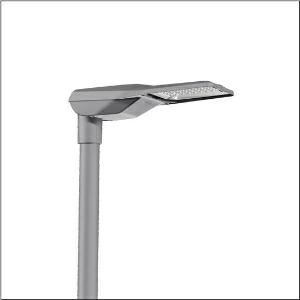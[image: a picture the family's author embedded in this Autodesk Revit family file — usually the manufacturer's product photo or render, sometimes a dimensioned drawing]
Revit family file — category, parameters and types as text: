
# Revit family: streetlight_sl_21_iq_mini___st0_8a_5xe2c41g08jb_e7d2
name_source: partatom
category: Lighting Fixtures
units: mm (PartAtom-declared; Revit-internal decimal feet)

## family parameters
Cut with Voids When Loaded = No
Host = Face
Light Source = No
Part Type = Normal
Room Calculation Point = No
Round Connector Dimension = Use Diameter
Shared = No

## types (1)
- --- (1 x LED, 11290 lm, 71.6 W, 4000K)
    Apparent Load = 72 VA
    CIE Flux Codes = 41 75 97 100 100
    Color Rendering = 70
    Color Temperature = 4000K
    Default Elevation = 1800 mm
    Description = Streetlight SL 21 iQ mini, mast luminaire, primary light control with lens, of PMMA, primary optical cover: cover, of toughened safety glass, transparent, light distribution: ST0.8a, light emission: direct distribution, primary light characteristic: asymmetric, installation type: post-top, side-entry, LED, High Power LED, rated luminous flux: 11.290lm, luminous efficacy: 158lm/W, light colour: 740, colour temperature: 4000K, control: Street-Remote, Auto-Match, Temp-Guard, Lumen-Switch, Night-Set, Smart-Wire, Light-Fading, Desk-Remote (wireless, voltage-free reading and setting of iQ features in the workshop via application-optimized NFC function/RFID function), optimised constant luminous flux control (CLO 2.0), presetting dimming linear, mains connection: 220..240V, AC, 50/60Hz, start of lifetime: 72W, end of service life: 75W, reduction: 33W, luminaire housing, of diecast aluminium, powder-coated, Siteco® metallic grey (DB 702S), corrosivity category C5 mid according to DIN EN ISO 12944, please order mast flange separately, inclination adjustable: 0°, 5°, 10°, 15°, sealing non-destructively replaceable, multi-level sealing system, length: 628mm, width: 235mm, height: 110mm, mast flange for spigot size: 42mm (side-entry): 5XC10008XM4, 60/48mm (side-entry/post-top): 5XC10108XM2, 76/60mm (side-entry/post-top): 5XC10108XM1, protection rating (complete): IP66, insulation class (complete): insulation class II (safety insulation), certification: CE, ENEC, ENEC+, VDE, impact resistance: IK09, permissible operating ambient temperature for outdoor applications: -40..+50°C, standard-compliant lighting for roads and squares, packaging unit: 1 piece

Light Distribution: ST0.8a
    Height = 110 mm
    Lamp = 1 x LED
    Lamp Light Flux = 11290 lm
    Lamp Power = 71.6 W
    Lamp count = 1
    Length = 625 mm
    Luminous efficacy = 158 lm/W
    Manufacturer = Siteco
    ModVariant = No
    Model = 5XE2C41G08JB
    Number of Poles = 1
    OnlyDefault = Yes
    Power Factor = 1
    Product Name = Streetlight SL 21 iQ mini | ST0.8a
    Product group = mast luminaire | pylon top
    ProductGroupID = 6100
    Protection Class = Protection class II
    Protection Degree = IP 66
    RLX_Detail_Level = 1
    RLX_Emergency_Light_Flux = 0 lm
    RLX_Emergency_Type = 0
    RLX_Emergency_Type_DB = No
    RlxData = <blob elided: 93565 chars, md5=aacba4fa>
    Socket = socket
    Standby Power = 0 W
    System Light Flux = 11290 lm
    System Power = 72 W
    Type Comments = factory setting: luminous flux: 100 % | dim-lin: 254 | 746 mA
    Type Image = l_1003519.jpg
    URL = http://relux.com
    VarID = @adj_101773
    Voltage = 0 V
    Weight = 0.00 kg
    Width = 234 mm

## geometry (parser evidence)
native form markers: Blend x4, Sweep x11
no freeform markers — native parametric forms only
